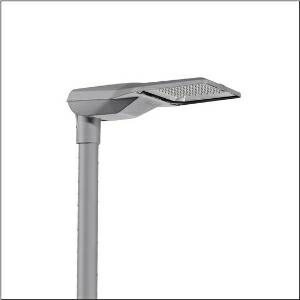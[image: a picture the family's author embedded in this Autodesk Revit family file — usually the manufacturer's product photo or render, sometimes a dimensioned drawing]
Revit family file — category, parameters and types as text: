
# Revit family: streetlight_sl_21_iq_midi___p0_8ab_5xe3r31d08nb_f4a3
name_source: partatom
category: Lighting Fixtures
units: mm (PartAtom-declared; Revit-internal decimal feet)

## family parameters
Cut with Voids When Loaded = No
Host = Face
Light Source = No
Part Type = Normal
Room Calculation Point = No
Round Connector Dimension = Use Diameter
Shared = No

## types (1)
- --- (1 x LED, 20170 lm, 155.5 W, 3000K)
    Apparent Load = 155 VA
    CIE Flux Codes = 39 72 97 100 100
    Color Rendering = 70
    Color Temperature = 3000K
    Default Elevation = 1800 mm
    Description = Streetlight SL 21 iQ midi, mast luminaire, primary light control with lens, of PMMA, primary optical cover: cover, of toughened safety glass, transparent, light distribution: P0.8aB, light emission: direct distribution, primary light characteristic: asymmetric, installation type: post-top, side-entry, LED, High Power LED, rated luminous flux: 20.170lm, luminous efficacy: 130lm/W, light colour: 730, colour temperature: 3000K, control gear: iQ-Comfort, control: pre-setting: linear dimming characteristic, Auto-Match, Temp-Guard, Lumen-Switch, Night-Set, Smart-Wire, Light-Fading, Desk-Remote (wireless, voltage-free reading and setting of iQ features in the workshop via application-optimized NFC function/RFID function), optimised constant luminous flux control (CLO 2.0), mains connection: 230..240V, AC, 50/60Hz, start of lifetime: 156W, end of service life: 162W, reduction: 69W, luminaire housing, of diecast aluminium, powder-coated, Siteco® metallic grey (DB 702S), corrosivity category C5 mid according to DIN EN ISO 12944, please order mast flange separately, inclination adjustable: 0°, 5°, 10°, 15°, sealing non-destructively replaceable, multi-level sealing system, length: 644mm, width: 335mm, height: 110mm, mast flange for spigot size: 42mm (side-entry): 5XC10008XM4, 60/48mm (side-entry/post-top): 5XC10108XM2, 76/60mm (side-entry/post-top): 5XC10108XM1, mounting height: 4..8m, protection rating (complete): IP66, insulation class (complete): insulation class II (safety insulation), certification: CE, ENEC, ENEC+, VDE, impact resistance: IK09, permissible operating ambient temperature for outdoor applications: -40..+50°C, standard-compliant lighting for roads and squares, packaging unit: 1 piece

Light Distribution: P0.8aB
    Height = 111 mm
    Lamp = 1 x LED
    Lamp Light Flux = 20170 lm
    Lamp Power = 155.5 W
    Lamp count = 1
    Length = 644 mm
    Luminous efficacy = 130 lm/W
    Manufacturer = Siteco
    ModVariant = No
    Model = 5XE3R31D08NB
    Number of Poles = 1
    OnlyDefault = Yes
    Power Factor = 1
    Product Name = Streetlight SL 21 iQ midi | P0.8aB
    Product group = mast luminaire | pylon top
    ProductGroupID = 6100
    Protection Class = Protection class II
    Protection Degree = IP 66
    RLX_Detail_Level = 1
    RLX_Emergency_Light_Flux = 0 lm
    RLX_Emergency_Type = 0
    RLX_Emergency_Type_DB = No
    RlxData = <blob elided: 90737 chars, md5=8df9eb5f>
    Socket = socket
    Standby Power = 0 W
    System Light Flux = 20170 lm
    System Power = 155 W
    Type Comments = factory setting: luminous flux: 100 % | dim-lin: 254 | 823 mA
    Type Image = l_1004298.jpg
    URL = http://relux.com
    VarID = @adj_068026
    Voltage = 0 V
    Weight = 0.00 kg
    Width = 336 mm

## geometry (parser evidence)
native form markers: Blend x4, Sweep x12
no freeform markers — native parametric forms only
